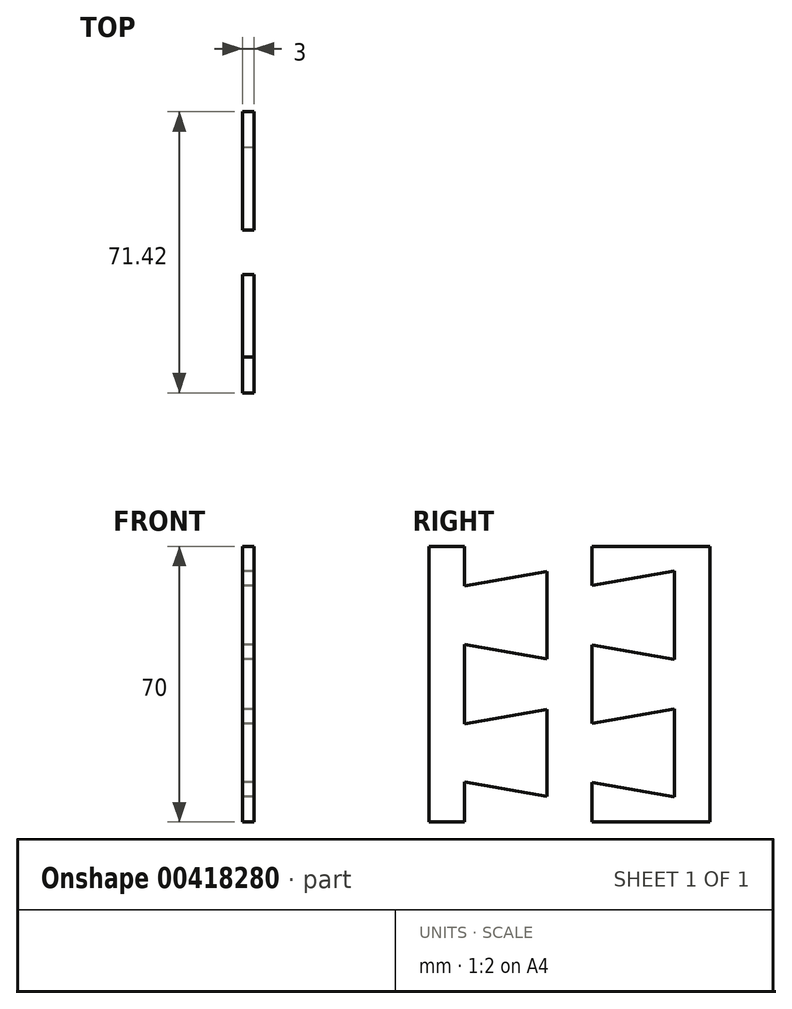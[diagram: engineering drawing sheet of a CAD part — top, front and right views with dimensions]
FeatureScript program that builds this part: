
annotation { "Feature Type Name" : "Feature", "Feature Type Description" : "" }
export const myFeature = defineFeature(function(context is Context, id is Id, definition is map)
    precondition{}
    {
        {
            var Q0;
            Q0=qCreatedBy(makeId("Right.planeOp"),FACE);
            var sketch = newSketch(context, id + "F0", { "sketchPlane" : qUnion([Q0])});
            skLineSegment(sketch, "E0", {"start": v(0, 0) * mm, "end": v(0, 10) * mm});
            skLineSegment(sketch, "E1", {"start": v(0, 10) * mm, "end": v(20.94, 6.3) * mm});
            skLineSegment(sketch, "E2", {"start": v(20.94, 6.3) * mm, "end": v(20.94, 28.7) * mm});
            skLineSegment(sketch, "E3", {"start": v(20.94, 28.7) * mm, "end": v(0, 25) * mm});
            skLineSegment(sketch, "E4", {"start": v(0, 25) * mm, "end": v(0, 35) * mm});
            skLineSegment(sketch, "E5", {"start": v(0, 35) * mm, "end": v(75.7, 35) * mm, "construction": true});
            skLineSegment(sketch, "E6.MirrorCS", {"start": v(0, 45) * mm, "end": v(0, 35) * mm});
            skLineSegment(sketch, "E7.MirrorCS", {"start": v(20.94, 41.3) * mm, "end": v(0, 45) * mm});
            skLineSegment(sketch, "E8.MirrorCS", {"start": v(20.94, 63.7) * mm, "end": v(20.94, 41.3) * mm});
            skLineSegment(sketch, "E9.MirrorCS", {"start": v(0, 60) * mm, "end": v(20.94, 63.7) * mm});
            skLineSegment(sketch, "E10.MirrorCS", {"start": v(0, 70) * mm, "end": v(0, 60) * mm});
            skLineSegment(sketch, "E11", {"start": v(0, 0) * mm, "end": v(30, 0) * mm});
            skLineSegment(sketch, "E12", {"start": v(30, 0) * mm, "end": v(30, 70) * mm});
            skLineSegment(sketch, "E13", {"start": v(30, 70) * mm, "end": v(0, 70) * mm});
            skLineSegment(sketch, "E14", {"start": v(-32.36, 0) * mm, "end": v(-32.36, 10.1) * mm});
            skLineSegment(sketch, "E15", {"start": v(-11.43, 28.6) * mm, "end": v(-32.36, 24.9) * mm});
            skLineSegment(sketch, "E16", {"start": v(-32.36, 24.9) * mm, "end": v(-32.36, 35) * mm});
            skLineSegment(sketch, "E17", {"start": v(0, 25) * mm, "end": v(0, 10) * mm, "construction": true});
            skLineSegment(sketch, "E18", {"start": v(-32.36, 10.1) * mm, "end": v(-11.43, 6.4) * mm});
            skLineSegment(sketch, "E19", {"start": v(-11.43, 6.4) * mm, "end": v(-11.43, 28.6) * mm});
            skLineSegment(sketch, "E20", {"start": v(-32.36, 24.9) * mm, "end": v(-32.36, 10.1) * mm, "construction": true});
            skLineSegment(sketch, "E21", {"start": v(0, 35) * mm, "end": v(-81.9, 35) * mm, "construction": true});
            skLineSegment(sketch, "E22.MirrorCS", {"start": v(-32.36, 45.1) * mm, "end": v(-32.36, 35) * mm});
            skLineSegment(sketch, "E23.MirrorCS", {"start": v(-11.43, 41.4) * mm, "end": v(-32.36, 45.1) * mm});
            skLineSegment(sketch, "E24.MirrorCS", {"start": v(-11.43, 63.6) * mm, "end": v(-11.43, 41.4) * mm});
            skLineSegment(sketch, "E25.MirrorCS", {"start": v(-32.36, 59.9) * mm, "end": v(-11.43, 63.6) * mm});
            skLineSegment(sketch, "E26.MirrorCS", {"start": v(-32.36, 70) * mm, "end": v(-32.36, 59.9) * mm});
            skLineSegment(sketch, "E27", {"start": v(-32.36, 0) * mm, "end": v(-41.42, 0) * mm});
            skLineSegment(sketch, "E28", {"start": v(-41.42, 0) * mm, "end": v(-41.42, 70) * mm});
            skLineSegment(sketch, "E29", {"start": v(-41.42, 70) * mm, "end": v(-32.36, 70) * mm});
            skSolve(sketch);
        }
        {
            var Q0;
            Q0=makeQuery(id+"F0.imprint","IMPRINT",FACE,{"disambiguationData":[TD([[makeQuery(id+"F0.imprint","IMPRINT",EDGE,{"derivedFrom":sQuery(id+"F0.wireOp",EDGE,"E14")}),1.0]])]});
            var Q1;
            Q1=makeQuery(id+"F0.imprint","IMPRINT",FACE,{"disambiguationData":[TD([[makeQuery(id+"F0.imprint","IMPRINT",EDGE,{"derivedFrom":sQuery(id+"F0.wireOp",EDGE,"E0")}),-1.0]])]});
            extrude(context, id + "F1", {"entities" : qUnion([Q0, Q1]), "depth" : 3 * mm});
        }
    });
